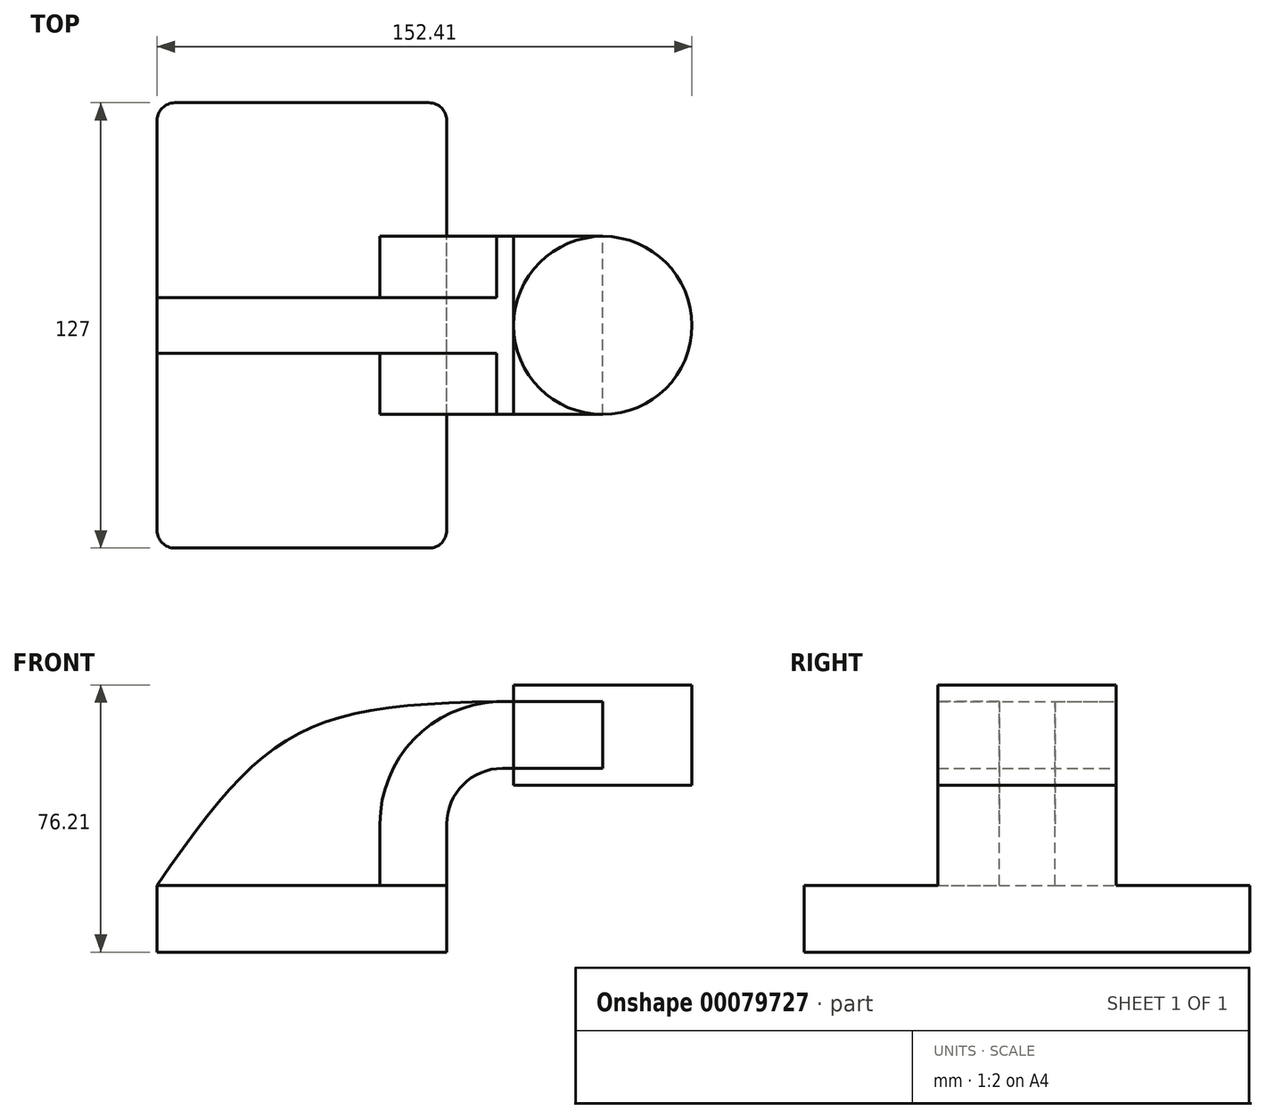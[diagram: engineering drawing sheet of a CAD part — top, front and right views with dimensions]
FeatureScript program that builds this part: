
annotation { "Feature Type Name" : "Feature", "Feature Type Description" : "" }
export const myFeature = defineFeature(function(context is Context, id is Id, definition is map)
    precondition{}
    {
        {
            var Q0;
            Q0=qCreatedBy(makeId("Front.planeOp"),FACE);
            var sketch = newSketch(context, id + "F0", { "sketchPlane" : qUnion([Q0])});
            skLineSegment(sketch, "E0.bottom", {"start": v(41.27, -9.52) * mm, "end": v(-41.28, -9.52) * mm});
            skLineSegment(sketch, "E0.top", {"start": v(41.27, 9.53) * mm, "end": v(-41.28, 9.53) * mm});
            skLineSegment(sketch, "E0.left", {"start": v(41.27, -9.52) * mm, "end": v(41.27, 9.53) * mm});
            skLineSegment(sketch, "E0.right", {"start": v(-41.28, -9.53) * mm, "end": v(-41.28, 9.53) * mm});
            skPoint(sketch, "E0.middle", {"position": v(0, 0) * mm});
            skLineSegment(sketch, "E1.bottom", {"start": v(111.12, 38.1) * mm, "end": v(60.33, 38.1) * mm});
            skLineSegment(sketch, "E1.top", {"start": v(111.12, 66.68) * mm, "end": v(60.33, 66.68) * mm});
            skLineSegment(sketch, "E1.left", {"start": v(111.12, 38.1) * mm, "end": v(111.12, 66.68) * mm});
            skLineSegment(sketch, "E1.right", {"start": v(60.33, 38.1) * mm, "end": v(60.32, 66.68) * mm});
            skPoint(sketch, "E1.middle", {"position": v(85.72, 52.39) * mm});
            skLineSegment(sketch, "E2", {"start": v(41.27, 9.53) * mm, "end": v(41.27, 27) * mm});
            skArc(sketch, "E3", {"start": v(41.27, 27) * mm, "mid": v(45.92, 38.23) * mm, "end": v(57.15, 42.88) * mm});
            skLineSegment(sketch, "E4", {"start": v(57.15, 42.88) * mm, "end": v(85.72, 42.88) * mm});
            skLineSegment(sketch, "E5.0", {"start": v(57.15, 61.93) * mm, "end": v(85.72, 61.93) * mm});
            skArc(sketch, "E5.1", {"start": v(22.23, 27) * mm, "mid": v(32.45, 51.7) * mm, "end": v(57.15, 61.93) * mm});
            skLineSegment(sketch, "E5.2", {"start": v(22.22, 9.53) * mm, "end": v(22.22, 27) * mm});
            skLineSegment(sketch, "E6", {"start": v(85.72, 42.88) * mm, "end": v(85.72, 61.93) * mm});
            skFitSpline(sketch, "E7", {"points": [v(-41.28, 9.53) * mm, v(60.32, 61.93) * mm], "startDerivative": vector(92.1, 134.48) * mm, "endDerivative": vector(180.98, 0.8) * mm});
            skLineSegment(sketch, "E8", {"start": v(85.72, 38.1) * mm, "end": v(85.72, 66.68) * mm});
            skSolve(sketch);
        }
        {
            var Q0;
            Q0=makeQuery(id+"F0.imprint","IMPRINT",FACE,{"disambiguationData":[TD([[makeQuery(id+"F0.imprint","IMPRINT",EDGE,{"derivedFrom":sQuery(id+"F0.wireOp",EDGE,"E0.bottom")}),-1.0]])]});
            extrude(context, id + "F1", {"entities" : qUnion([Q0]), "endBound" : BoundingType.SYMMETRIC, "depth" : 127 * mm});
        }
        {
            var Q0;
            {var subQ1=sQuery(id+"F0.wireOp",EDGE,"E2");Q0=makeQuery(id+"F0.imprint","IMPRINT",FACE,{"disambiguationData":[TD([[makeQuery(id+"F0.imprint","IMPRINT",EDGE,{"derivedFrom":subQ1}),1.0]])]});}
            extrude(context, id + "F2", {"entities" : qUnion([Q0]), "operationType" : NewBodyOperationType.ADD, "endBound" : BoundingType.SYMMETRIC, "depth" : 50.8 * mm});
        }
        {
            var Q0;
            {var subQ3=sQuery(id+"F0.wireOp",EDGE,"E5.2");Q0=makeQuery(id+"F0.imprint","IMPRINT",FACE,{"disambiguationData":[TD([[makeQuery(id+"F0.imprint","IMPRINT",EDGE,{"derivedFrom":subQ3}),1.0]])]});}
            extrude(context, id + "F3", {"entities" : qUnion([Q0]), "operationType" : NewBodyOperationType.ADD, "endBound" : BoundingType.SYMMETRIC, "depth" : 15.88 * mm});
        }
        {
            var Q0;
            {var subQ4=sQuery(id+"F0.wireOp",EDGE,"E1.left");Q0=makeQuery(id+"F0.imprint","IMPRINT",FACE,{"disambiguationData":[TD([[makeQuery(id+"F0.imprint","IMPRINT",EDGE,{"derivedFrom":subQ4}),1.0]])]});}
            var Q1;
            Q1=sQuery(id+"F0.wireOp",EDGE,"E8");
            revolve(context, id + "F4", {"operationType" : NewBodyOperationType.ADD, "entities" : qUnion([Q0]), "axis" : qUnion([Q1]), "revolveType" : RevolveType.FULL});
        }
        {
            var Q0;
            Q0=makeQuery(id+"F1.opExtrude","CAP_EDGE",EDGE,{"disambiguationData":[OSD([sQuery(id+"F0.wireOp",EDGE,"E0.right")])],"isStart":false});
            var Q1;
            Q1=makeQuery(id+"F1.opExtrude","CAP_EDGE",EDGE,{"disambiguationData":[OSD([sQuery(id+"F0.wireOp",EDGE,"E0.left")])],"isStart":false});
            var Q2;
            Q2=makeQuery(id+"F1.opExtrude","CAP_EDGE",EDGE,{"disambiguationData":[OSD([sQuery(id+"F0.wireOp",EDGE,"E0.right")])],"isStart":true});
            var Q3;
            Q3=makeQuery(id+"F1.opExtrude","CAP_EDGE",EDGE,{"disambiguationData":[OSD([sQuery(id+"F0.wireOp",EDGE,"E0.left")])],"isStart":true});
            fillet(context, id + "F5", {"entities" : qUnion([Q0, Q1, Q2, Q3]), "radius" : 5.08 * mm, "tangentPropagation" : true, "allowEdgeOverflow" : false});
        }
        {
            var Q0;
            Q0=makeQuery(id+"F2.opExtrude","SWEPT_FACE",FACE,{"disambiguationData":[OSD([sQuery(id+"F0.wireOp",EDGE,"E1.right")])]});
            extrude(context, id + "F6", {"entities" : qUnion([Q0]), "depth" : 25.4 * mm});
        }
    });
